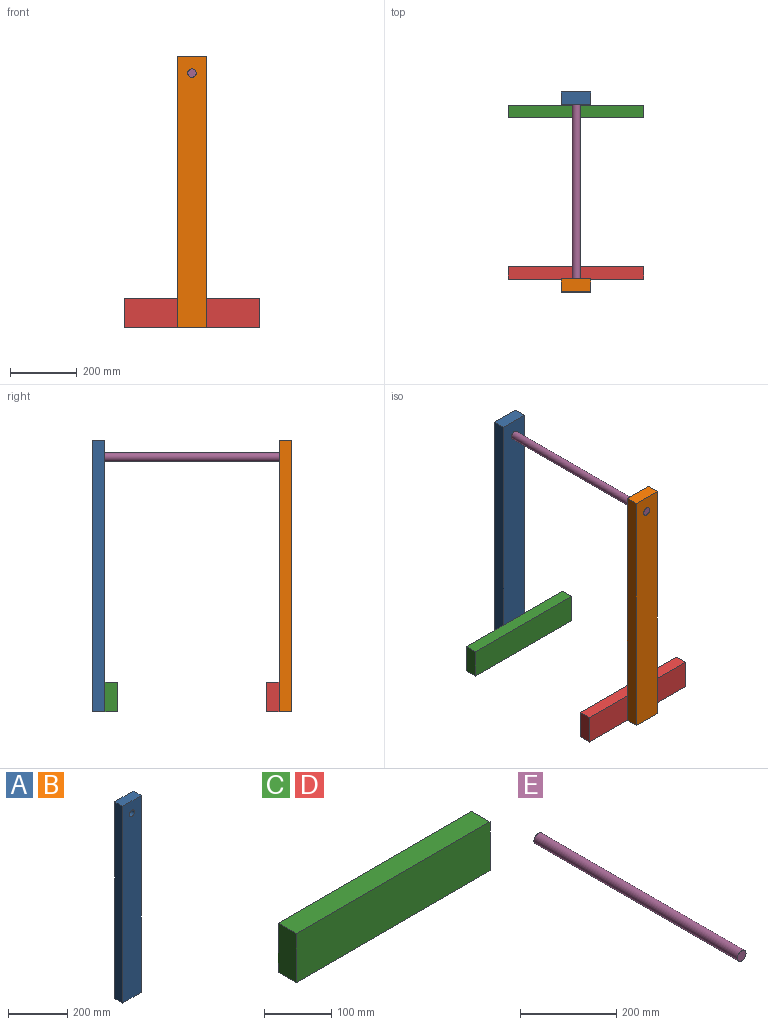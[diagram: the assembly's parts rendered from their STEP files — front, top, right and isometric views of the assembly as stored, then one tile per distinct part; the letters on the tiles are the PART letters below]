
ASSEMBLY  parts=5 mates=4
PART A: 7 faces, bbox 88.9x38.1x812.8 mm
  f0: plane 88.9x38.1mm, normal (0,0,-1), area 3387.1mm2, adj f1,f4,f5,f6
  f1: plane 812.8x38.1mm, normal (1,0,0), area 30967.7mm2, adj f0,f2,f5,f6
  f2: plane 88.9x38.1mm, normal (0,0,1), area 3387.1mm2, adj f1,f4,f5,f6
  f3: cylinder r=12.7mm len=38.1mm, axis (0,1,0), area 3040.2mm2, adj f5,f6
  f4: plane 812.8x38.1mm, normal (-1,0,0), area 30967.7mm2, adj f0,f2,f5,f6
  f5: plane 812.8x88.9mm, normal (0,-1,0), area 71751.2mm2, adj f0,f1,f2,f3,f4
  f6: plane 812.8x88.9mm, normal (0,1,0), area 71751.2mm2, adj f0,f1,f2,f3,f4
PART B: same geometry as A
PART C: 6 faces, bbox 406.4x38.1x88.9 mm
  f0: plane 406.4x38.1mm, normal (0,0,1), area 15483.8mm2, adj f1,f3,f4,f5
  f1: plane 88.9x38.1mm, normal (-1,0,0), area 3387.1mm2, adj f0,f2,f4,f5
  f2: plane 406.4x38.1mm, normal (0,0,-1), area 15483.8mm2, adj f1,f3,f4,f5
  f3: plane 88.9x38.1mm, normal (1,0,0), area 3387.1mm2, adj f0,f2,f4,f5
  f4: plane 406.4x88.9mm, normal (0,-1,0), area 36129mm2, adj f0,f1,f2,f3
  f5: plane 406.4x88.9mm, normal (0,1,0), area 36129mm2, adj f0,f1,f2,f3
PART D: same geometry as C
PART E: 3 faces, bbox 25.4x596.9x25.4 mm
  f0: cylinder r=12.7mm len=596.9mm, axis (0,1,0), area 47630.5mm2, adj f1,f2
  f1: plane 25.4x25.4mm, normal (0,-1,0), area 506.7mm2, adj f0
  f2: plane 25.4x25.4mm, normal (0,1,0), area 506.7mm2, adj f0
PLACE A t=(96.76,-18.07,-348.53)mm
PLACE B t=(96.76,-576.87,-348.53)mm
PLACE C t=(96.76,-56.17,-710.48)mm
PLACE D t=(96.76,-538.77,-710.48)mm
PLACE E t=(96.76,-18.07,7.07)mm
MATE fastened E.f0 <-> A.f3  axis (0,1,0) through (96.76,-18.07,7.07)mm
MATE fastened E.f0 <-> B.f3  axis (0,-1,0) through (96.76,-614.97,7.07)mm
MATE fastened C.f5 <-> A.f5  axis (0,1,0) through (96.76,-56.17,-754.93)mm
MATE fastened D.f4 <-> B.f6  axis (0,-1,0) through (96.76,-576.87,-754.93)mm
